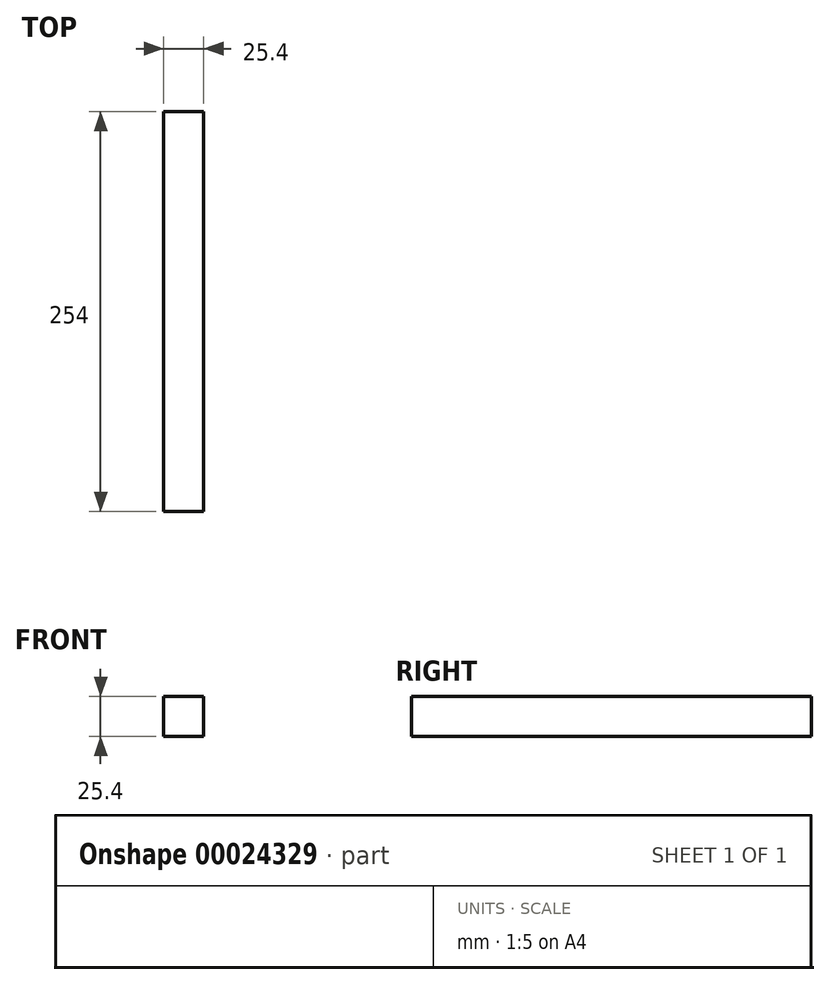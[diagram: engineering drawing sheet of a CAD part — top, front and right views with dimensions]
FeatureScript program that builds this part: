
annotation { "Feature Type Name" : "Feature", "Feature Type Description" : "" }
export const myFeature = defineFeature(function(context is Context, id is Id, definition is map)
    precondition{}
    {
        {
            var Q0;
            Q0=qCreatedBy(makeId("Top.planeOp"),FACE);
            var sketch = newSketch(context, id + "F0", { "sketchPlane" : qUnion([Q0])});
            skLineSegment(sketch, "E0", {"start": v(-156.7, 222.18) * mm, "end": v(-156.7, -31.82) * mm});
            skLineSegment(sketch, "E1", {"start": v(-156.7, -31.82) * mm, "end": v(-131.3, -31.82) * mm});
            skLineSegment(sketch, "E2", {"start": v(-131.3, -31.82) * mm, "end": v(-131.3, 222.18) * mm});
            skLineSegment(sketch, "E3", {"start": v(-131.3, 222.18) * mm, "end": v(-156.7, 222.18) * mm});
            skSolve(sketch);
        }
        {
            var Q0;
            Q0 = qSketchRegion(id + "F0", true);
            extrude(context, id + "F1", {"entities" : qUnion([Q0]), "depth" : 25.4 * mm});
        }
    });
